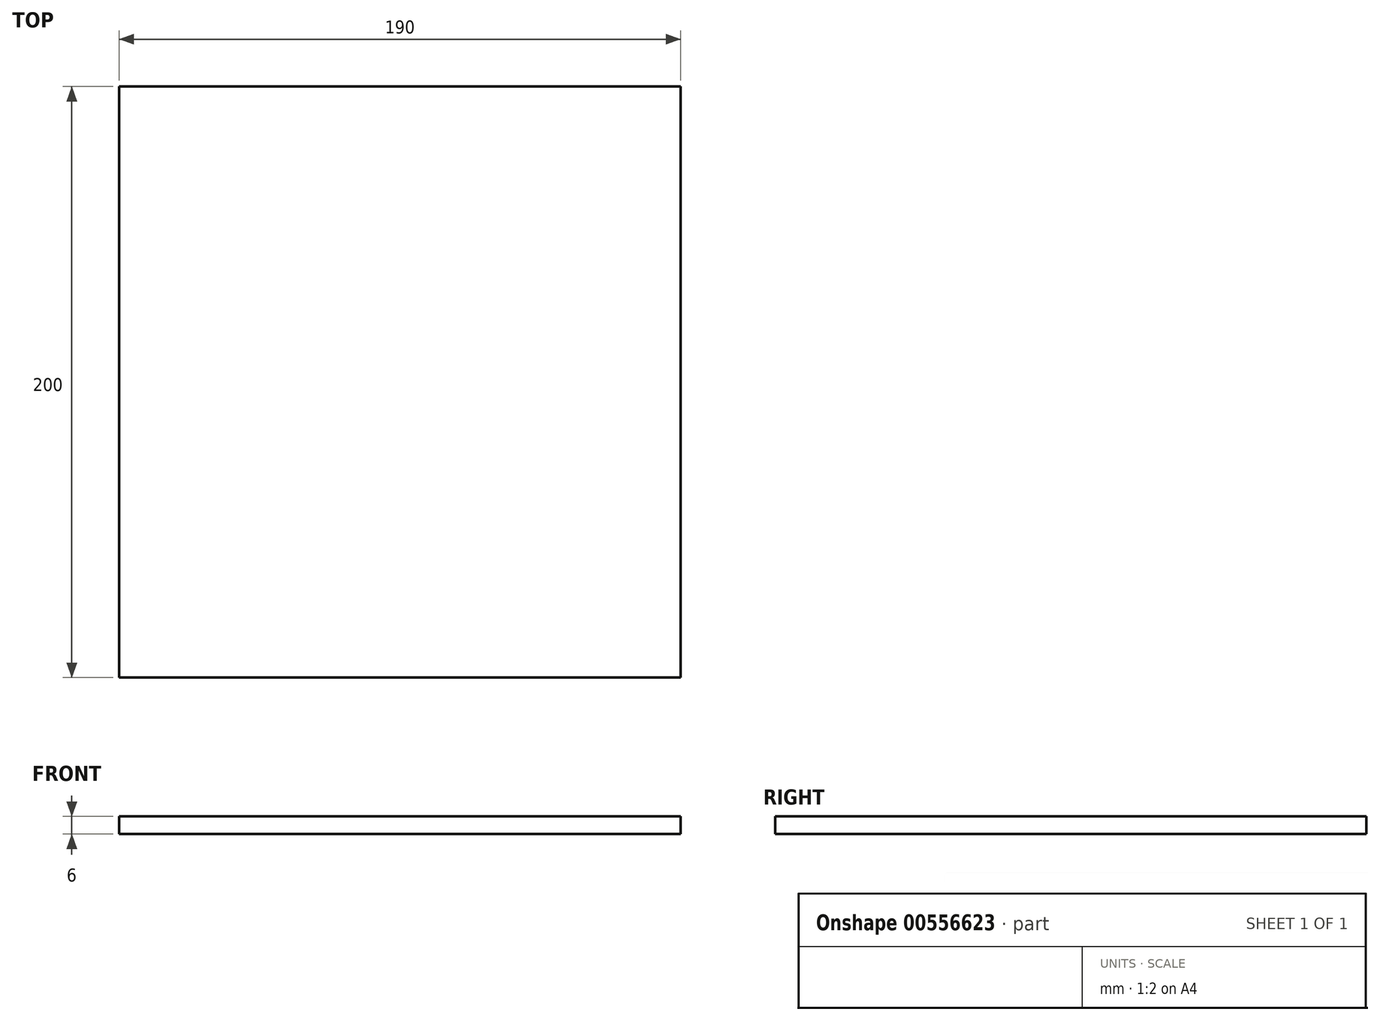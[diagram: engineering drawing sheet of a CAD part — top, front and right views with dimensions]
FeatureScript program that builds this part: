
annotation { "Feature Type Name" : "Feature", "Feature Type Description" : "" }
export const myFeature = defineFeature(function(context is Context, id is Id, definition is map)
    precondition{}
    {
        {
            var Q0;
            Q0=qCreatedBy(makeId("Top.planeOp"),FACE);
            var sketch = newSketch(context, id + "F0", { "sketchPlane" : qUnion([Q0])});
            skLineSegment(sketch, "E0", {"start": v(0, -73.23) * mm, "end": v(0, 126.77) * mm});
            skLineSegment(sketch, "E1", {"start": v(0, 126.77) * mm, "end": v(190, 126.77) * mm});
            skLineSegment(sketch, "E2", {"start": v(190, 126.77) * mm, "end": v(190, -73.23) * mm});
            skLineSegment(sketch, "E3", {"start": v(190, -73.23) * mm, "end": v(0, -73.23) * mm});
            skSolve(sketch);
        }
        {
            var Q0;
            Q0=makeQuery(id+"F0.imprint","IMPRINT",FACE,{"disambiguationData":[TD([[makeQuery(id+"F0.imprint","IMPRINT",EDGE,{"derivedFrom":sQuery(id+"F0.wireOp",EDGE,"E0")}),-1.0]])]});
            extrude(context, id + "F1", {"entities" : qUnion([Q0]), "endBound" : BoundingType.SYMMETRIC, "depth" : 6 * mm, "offsetDistance" : 25 * mm});
        }
    });
